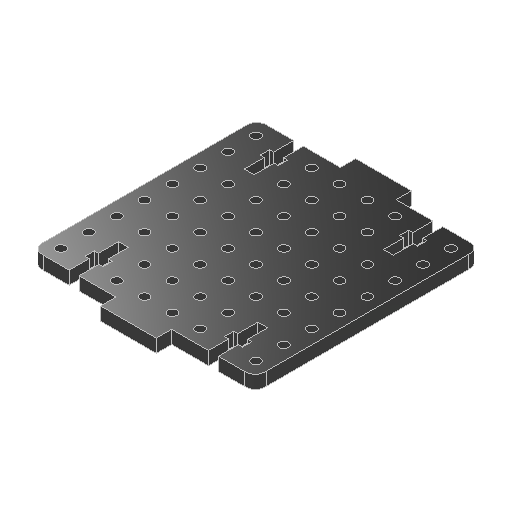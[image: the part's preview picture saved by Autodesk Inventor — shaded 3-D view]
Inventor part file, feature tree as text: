
AUTODESK INVENTOR PART (.ipt)
format: ipt  version: 2025 (Build 290162000, 162)  size: 272,384 bytes
history: native  units: mm
features: sketch x4, extrude x3, mirror x2, plane x1, fillet x1, hole x1, pattern_linear x1, projected_geometry x1
ambient origin geometry x8: Origin, YZ Plane, XZ Plane, XY Plane, X Axis, Y Axis, Z Axis, Center Point
bodies: Solid1 (feature_tree)
feature tree (14):
  extrude  "Extrusion1"  Depth=6.0mm
  plane  "Work Plane1"
  extrude  "Extrusion2"  Depth=6.0mm
  mirror  "Mirror1"
  extrude  "Extrusion3"  Depth=102.3mm
  fillet  "Fillet1"  Radius=7.0mm
  mirror  "Mirror2"
  hole  "Hole1"  [1 undecoded]
  pattern_linear  "Rectangular Pattern1"  Spacing1=0.0mm  [1 undecoded]
  sketch  "Sketch1"  dims[d1=6.0mm d2=0.0mm d3=6.7mm]
  sketch  "Sketch2"  dims[d4=4.25mm d5=6.0mm d6=4.0mm d7=2.0mm d8=90.0deg d9=8.0mm d10=20.594885mm d11=80.0mm d13=12.7mm d14=80.0mm d16=12.7mm]
  sketch  "Sketch3"  dims[d17=5.0mm d19=102.3mm d20=7.0mm]
  projected_geometry  "Projected Loop1"
  sketch  "Sketch4"  dims[d22=0.0mm d23=0.0mm d25=4.25mm d26=8.25mm d28=4.4958mm d29=0.0mm d30=0.0mm d31=25.4mm d32=22.5mm d39=101.6mm d40=6.35mm]
note: 2 required parameter values undecoded (feature->parameter linkage not recoverable at this tier; creation-order binding heuristic only, values carry confidence <= 0.55)
